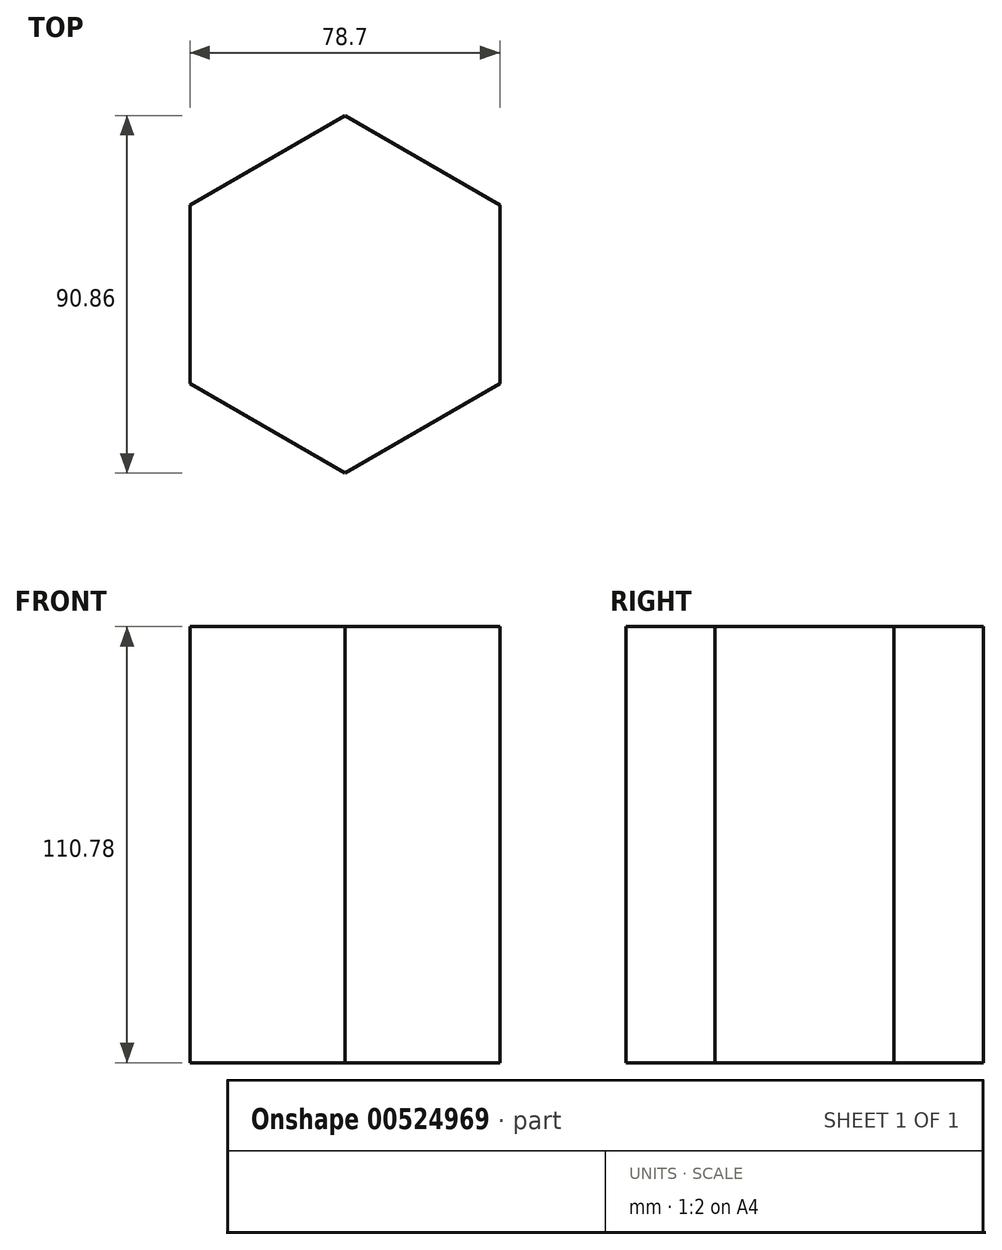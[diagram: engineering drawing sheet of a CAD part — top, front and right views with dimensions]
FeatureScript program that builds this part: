
annotation { "Feature Type Name" : "Feature", "Feature Type Description" : "" }
export const myFeature = defineFeature(function(context is Context, id is Id, definition is map)
    precondition{}
    {
        {
            var Q0;
            Q0=qCreatedBy(makeId("Top.planeOp"),FACE);
            var sketch = newSketch(context, id + "F0", { "sketchPlane" : qUnion([Q0])});
            skCircle(sketch, "E0.cCircle", {"center": v(0, 0) * mm, "radius": 39.35 * mm, "construction": true});
            skLineSegment(sketch, "E0.0", {"start": v(-39.35, -22.72) * mm, "end": v(-39.35, 22.72) * mm});
            skLineSegment(sketch, "E0.1", {"start": v(-39.35, 22.72) * mm, "end": v(0, 45.43) * mm});
            skLineSegment(sketch, "E0.2", {"start": v(0, 45.43) * mm, "end": v(39.35, 22.72) * mm});
            skLineSegment(sketch, "E0.3", {"start": v(39.35, 22.72) * mm, "end": v(39.35, -22.72) * mm});
            skLineSegment(sketch, "E0.4", {"start": v(39.35, -22.72) * mm, "end": v(0, -45.43) * mm});
            skLineSegment(sketch, "E0.5", {"start": v(0, -45.43) * mm, "end": v(-39.35, -22.72) * mm});
            skPoint(sketch, "E0.0.midPoint", {"position": v(-39.35, 0) * mm});
            skSolve(sketch);
        }
        {
            var Q0;
            Q0=makeQuery(id+"F0.imprint","IMPRINT",FACE,{"disambiguationData":[TD([[makeQuery(id+"F0.imprint","IMPRINT",EDGE,{"derivedFrom":sQuery(id+"F0.wireOp",EDGE,"E0.0")}),-1.0]])]});
            extrude(context, id + "F1", {"entities" : qUnion([Q0]), "depth" : 110.78 * mm, "offsetDistance" : 25 * mm});
        }
    });
